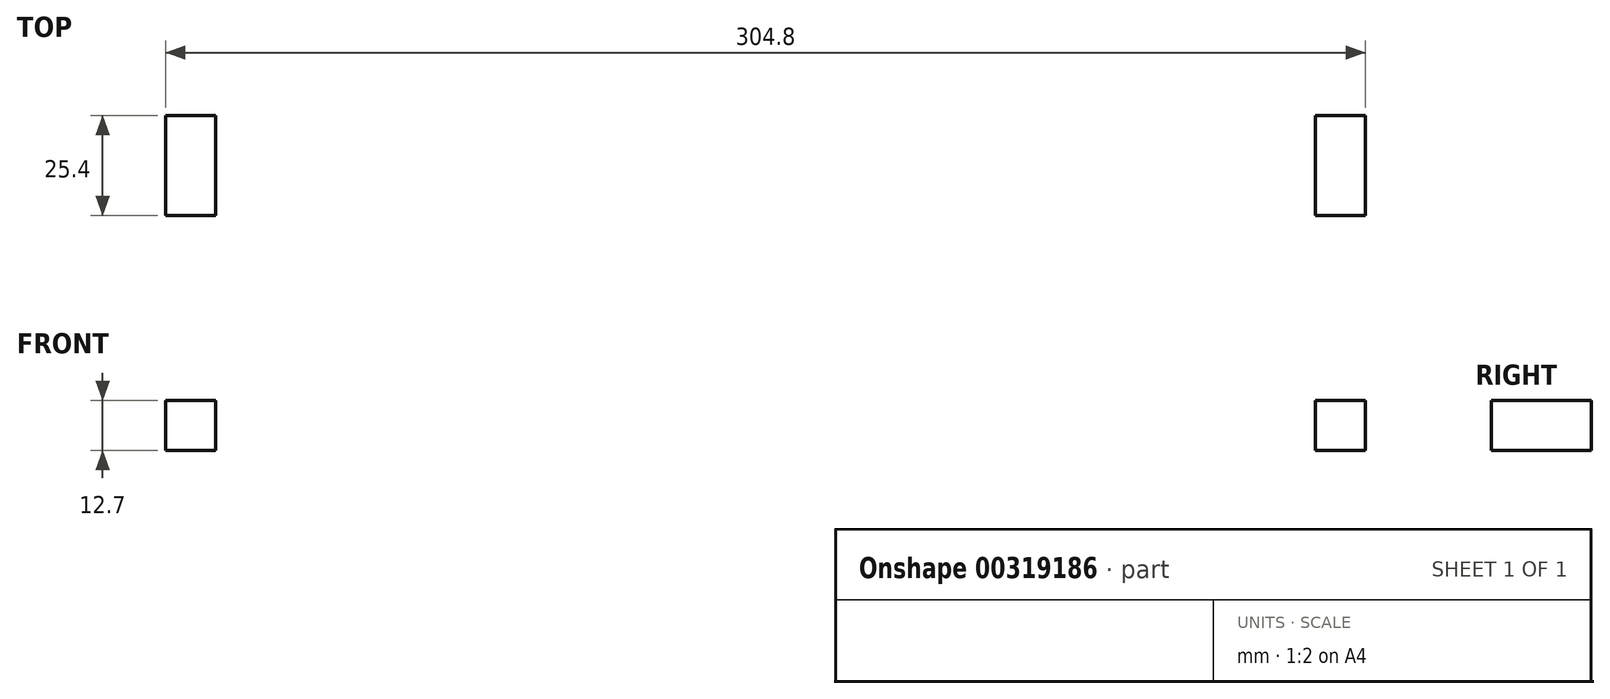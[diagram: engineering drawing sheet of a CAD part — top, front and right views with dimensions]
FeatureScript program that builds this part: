
annotation { "Feature Type Name" : "Feature", "Feature Type Description" : "" }
export const myFeature = defineFeature(function(context is Context, id is Id, definition is map)
    precondition{}
    {
        {
            var Q0;
            Q0=qCreatedBy(makeId("Top.planeOp"),FACE);
            var sketch = newSketch(context, id + "F0", { "sketchPlane" : qUnion([Q0])});
            skLineSegment(sketch, "E0.bottom", {"start": v(-152.4, 152.4) * mm, "end": v(152.4, 152.4) * mm});
            skLineSegment(sketch, "E0.top", {"start": v(-152.4, -152.4) * mm, "end": v(152.4, -152.4) * mm});
            skLineSegment(sketch, "E0.left", {"start": v(-152.4, 152.4) * mm, "end": v(-152.4, -152.4) * mm});
            skLineSegment(sketch, "E0.right", {"start": v(152.4, 152.4) * mm, "end": v(152.4, -152.4) * mm});
            skPoint(sketch, "E0.middle", {"position": v(0, 0) * mm});
            skLineSegment(sketch, "E1.bottom", {"start": v(152.4, -152.4) * mm, "end": v(139.7, -152.4) * mm});
            skLineSegment(sketch, "E1.top", {"start": v(152.4, -127) * mm, "end": v(139.7, -127) * mm});
            skLineSegment(sketch, "E1.left", {"start": v(152.4, -152.4) * mm, "end": v(152.4, -127) * mm});
            skLineSegment(sketch, "E1.right", {"start": v(139.7, -152.4) * mm, "end": v(139.7, -127) * mm});
            skLineSegment(sketch, "E2.bottom", {"start": v(-152.4, -152.4) * mm, "end": v(-139.7, -152.4) * mm});
            skLineSegment(sketch, "E2.top", {"start": v(-152.4, -127) * mm, "end": v(-139.7, -127) * mm});
            skLineSegment(sketch, "E2.left", {"start": v(-152.4, -152.4) * mm, "end": v(-152.4, -127) * mm});
            skLineSegment(sketch, "E2.right", {"start": v(-139.7, -152.4) * mm, "end": v(-139.7, -127) * mm});
            skLineSegment(sketch, "E3.0.1.0", {"start": v(152.4, -76.2) * mm, "end": v(139.7, -76.2) * mm});
            skLineSegment(sketch, "E3.0.1.1", {"start": v(139.7, -101.6) * mm, "end": v(139.7, -76.2) * mm});
            skLineSegment(sketch, "E3.0.1.2", {"start": v(152.4, -101.6) * mm, "end": v(139.7, -101.6) * mm});
            skLineSegment(sketch, "E3.0.1.3", {"start": v(152.4, -101.6) * mm, "end": v(152.4, -76.2) * mm});
            skLineSegment(sketch, "E3.0.1.4", {"start": v(-152.4, -76.2) * mm, "end": v(-139.7, -76.2) * mm});
            skLineSegment(sketch, "E3.0.1.5", {"start": v(-139.7, -101.6) * mm, "end": v(-139.7, -76.2) * mm});
            skLineSegment(sketch, "E3.0.1.6", {"start": v(-152.4, -101.6) * mm, "end": v(-139.7, -101.6) * mm});
            skLineSegment(sketch, "E3.0.1.7", {"start": v(-152.4, -101.6) * mm, "end": v(-152.4, -76.2) * mm});
            skLineSegment(sketch, "E3.0.2.0", {"start": v(152.4, -25.4) * mm, "end": v(139.7, -25.4) * mm});
            skLineSegment(sketch, "E3.0.2.1", {"start": v(139.7, -50.8) * mm, "end": v(139.7, -25.4) * mm});
            skLineSegment(sketch, "E3.0.2.2", {"start": v(152.4, -50.8) * mm, "end": v(139.7, -50.8) * mm});
            skLineSegment(sketch, "E3.0.2.3", {"start": v(152.4, -50.8) * mm, "end": v(152.4, -25.4) * mm});
            skLineSegment(sketch, "E3.0.2.4", {"start": v(-152.4, -25.4) * mm, "end": v(-139.7, -25.4) * mm});
            skLineSegment(sketch, "E3.0.2.5", {"start": v(-139.7, -50.8) * mm, "end": v(-139.7, -25.4) * mm});
            skLineSegment(sketch, "E3.0.2.6", {"start": v(-152.4, -50.8) * mm, "end": v(-139.7, -50.8) * mm});
            skLineSegment(sketch, "E3.0.2.7", {"start": v(-152.4, -50.8) * mm, "end": v(-152.4, -25.4) * mm});
            skLineSegment(sketch, "E3.0.3.0", {"start": v(152.4, 25.4) * mm, "end": v(139.7, 25.4) * mm});
            skLineSegment(sketch, "E3.0.3.1", {"start": v(139.7, 0) * mm, "end": v(139.7, 25.4) * mm});
            skLineSegment(sketch, "E3.0.3.2", {"start": v(152.4, 0) * mm, "end": v(139.7, 0) * mm});
            skLineSegment(sketch, "E3.0.3.3", {"start": v(152.4, 0) * mm, "end": v(152.4, 25.4) * mm});
            skLineSegment(sketch, "E3.0.3.4", {"start": v(-152.4, 25.4) * mm, "end": v(-139.7, 25.4) * mm});
            skLineSegment(sketch, "E3.0.3.5", {"start": v(-139.7, 0) * mm, "end": v(-139.7, 25.4) * mm});
            skLineSegment(sketch, "E3.0.3.6", {"start": v(-152.4, 0) * mm, "end": v(-139.7, 0) * mm});
            skLineSegment(sketch, "E3.0.3.7", {"start": v(-152.4, 0) * mm, "end": v(-152.4, 25.4) * mm});
            skLineSegment(sketch, "E3.0.4.0", {"start": v(152.4, 76.2) * mm, "end": v(139.7, 76.2) * mm});
            skLineSegment(sketch, "E3.0.4.1", {"start": v(139.7, 50.8) * mm, "end": v(139.7, 76.2) * mm});
            skLineSegment(sketch, "E3.0.4.2", {"start": v(152.4, 50.8) * mm, "end": v(139.7, 50.8) * mm});
            skLineSegment(sketch, "E3.0.4.3", {"start": v(152.4, 50.8) * mm, "end": v(152.4, 76.2) * mm});
            skLineSegment(sketch, "E3.0.4.4", {"start": v(-152.4, 76.2) * mm, "end": v(-139.7, 76.2) * mm});
            skLineSegment(sketch, "E3.0.4.5", {"start": v(-139.7, 50.8) * mm, "end": v(-139.7, 76.2) * mm});
            skLineSegment(sketch, "E3.0.4.6", {"start": v(-152.4, 50.8) * mm, "end": v(-139.7, 50.8) * mm});
            skLineSegment(sketch, "E3.0.4.7", {"start": v(-152.4, 50.8) * mm, "end": v(-152.4, 76.2) * mm});
            skLineSegment(sketch, "E3.0.5.0", {"start": v(152.4, 127) * mm, "end": v(139.7, 127) * mm});
            skLineSegment(sketch, "E3.0.5.1", {"start": v(139.7, 101.6) * mm, "end": v(139.7, 127) * mm});
            skLineSegment(sketch, "E3.0.5.2", {"start": v(152.4, 101.6) * mm, "end": v(139.7, 101.6) * mm});
            skLineSegment(sketch, "E3.0.5.3", {"start": v(152.4, 101.6) * mm, "end": v(152.4, 127) * mm});
            skLineSegment(sketch, "E3.0.5.4", {"start": v(-152.4, 127) * mm, "end": v(-139.7, 127) * mm});
            skLineSegment(sketch, "E3.0.5.5", {"start": v(-139.7, 101.6) * mm, "end": v(-139.7, 127) * mm});
            skLineSegment(sketch, "E3.0.5.6", {"start": v(-152.4, 101.6) * mm, "end": v(-139.7, 101.6) * mm});
            skLineSegment(sketch, "E3.0.5.7", {"start": v(-152.4, 101.6) * mm, "end": v(-152.4, 127) * mm});
            skLineSegment(sketch, "E3.direction1", {"start": v(139.7, -127) * mm, "end": v(165.1, -127) * mm, "construction": true});
            skLineSegment(sketch, "E3.direction2", {"start": v(139.7, -127) * mm, "end": v(139.7, -76.2) * mm, "construction": true});
            skLineSegment(sketch, "E4.bottom", {"start": v(-114.3, 152.4) * mm, "end": v(-88.9, 152.4) * mm});
            skLineSegment(sketch, "E4.top", {"start": v(-114.3, 139.7) * mm, "end": v(-88.9, 139.7) * mm});
            skLineSegment(sketch, "E4.left", {"start": v(-114.3, 152.4) * mm, "end": v(-114.3, 139.7) * mm});
            skLineSegment(sketch, "E4.right", {"start": v(-88.9, 152.4) * mm, "end": v(-88.9, 139.7) * mm});
            skLineSegment(sketch, "E5.1.0.0", {"start": v(-63.5, 139.7) * mm, "end": v(-38.1, 139.7) * mm});
            skLineSegment(sketch, "E5.1.0.1", {"start": v(-63.5, 152.4) * mm, "end": v(-63.5, 139.7) * mm});
            skLineSegment(sketch, "E5.1.0.2", {"start": v(-38.1, 152.4) * mm, "end": v(-38.1, 139.7) * mm});
            skLineSegment(sketch, "E5.1.0.3", {"start": v(-63.5, 152.4) * mm, "end": v(-38.1, 152.4) * mm});
            skLineSegment(sketch, "E5.2.0.0", {"start": v(-12.7, 139.7) * mm, "end": v(12.7, 139.7) * mm});
            skLineSegment(sketch, "E5.2.0.1", {"start": v(-12.7, 152.4) * mm, "end": v(-12.7, 139.7) * mm});
            skLineSegment(sketch, "E5.2.0.2", {"start": v(12.7, 152.4) * mm, "end": v(12.7, 139.7) * mm});
            skLineSegment(sketch, "E5.2.0.3", {"start": v(-12.7, 152.4) * mm, "end": v(12.7, 152.4) * mm});
            skLineSegment(sketch, "E5.3.0.0", {"start": v(38.1, 139.7) * mm, "end": v(63.5, 139.7) * mm});
            skLineSegment(sketch, "E5.3.0.1", {"start": v(38.1, 152.4) * mm, "end": v(38.1, 139.7) * mm});
            skLineSegment(sketch, "E5.3.0.2", {"start": v(63.5, 152.4) * mm, "end": v(63.5, 139.7) * mm});
            skLineSegment(sketch, "E5.3.0.3", {"start": v(38.1, 152.4) * mm, "end": v(63.5, 152.4) * mm});
            skLineSegment(sketch, "E5.4.0.0", {"start": v(88.9, 139.7) * mm, "end": v(114.3, 139.7) * mm});
            skLineSegment(sketch, "E5.4.0.1", {"start": v(88.9, 152.4) * mm, "end": v(88.9, 139.7) * mm});
            skLineSegment(sketch, "E5.4.0.2", {"start": v(114.3, 152.4) * mm, "end": v(114.3, 139.7) * mm});
            skLineSegment(sketch, "E5.4.0.3", {"start": v(88.9, 152.4) * mm, "end": v(114.3, 152.4) * mm});
            skLineSegment(sketch, "E5.direction1", {"start": v(-114.3, 139.7) * mm, "end": v(-63.5, 139.7) * mm, "construction": true});
            skSolve(sketch);
        }
        {
            var Q0;
            Q0=makeQuery(id+"F0.imprint","IMPRINT",FACE,{"disambiguationData":[TD([[makeQuery(id+"F0.imprint","IMPRINT",EDGE,{"derivedFrom":sQuery(id+"F0.wireOp",EDGE,"E0.top")}),1.0]])]});
            extrude(context, id + "F1", {"entities" : qUnion([Q0]), "depth" : 12.7 * mm});
        }
    });
